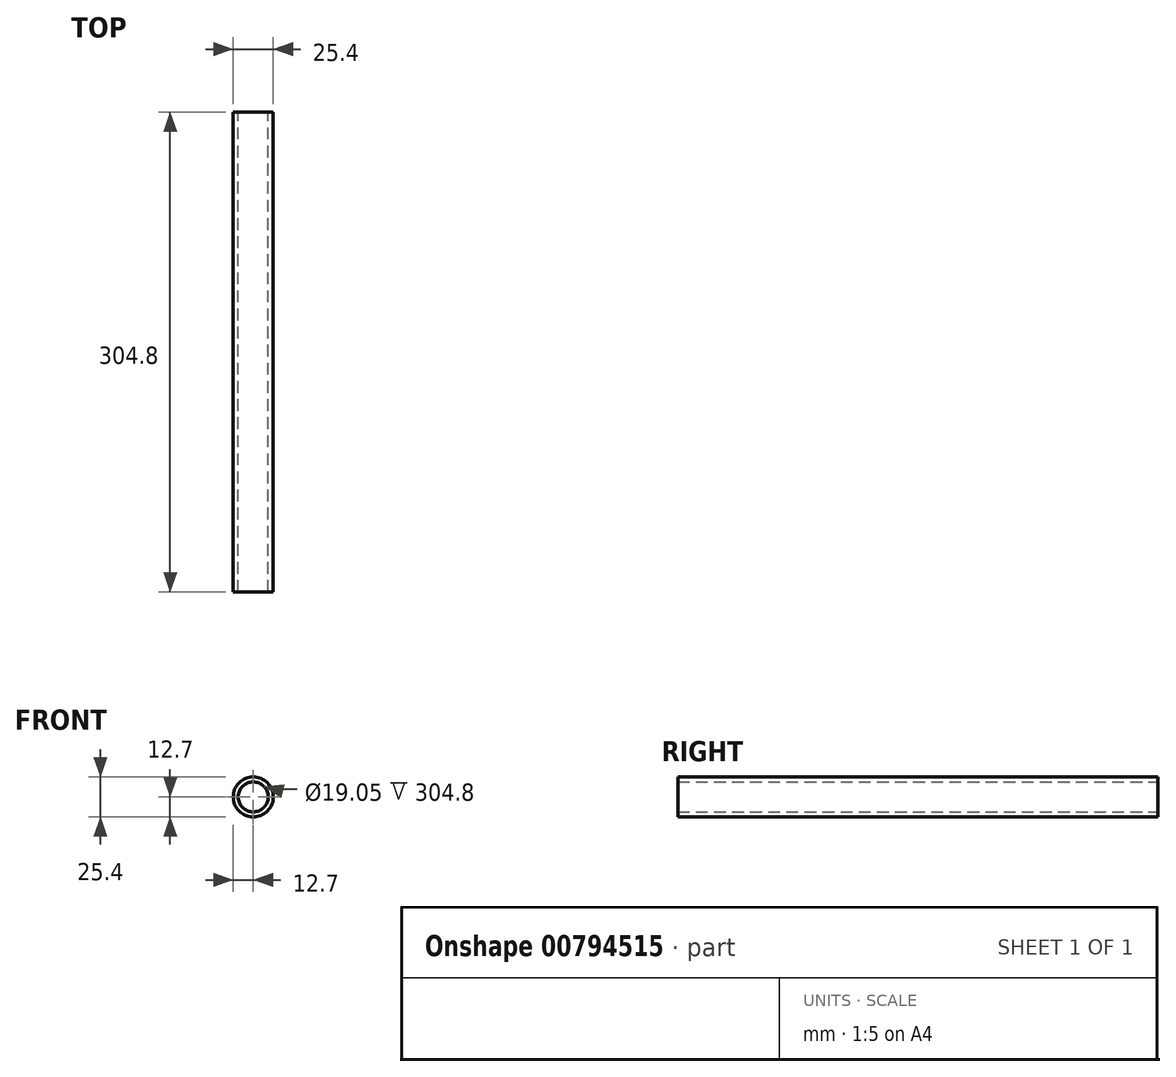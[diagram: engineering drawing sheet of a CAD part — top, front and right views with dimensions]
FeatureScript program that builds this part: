
annotation { "Feature Type Name" : "Feature", "Feature Type Description" : "" }
export const myFeature = defineFeature(function(context is Context, id is Id, definition is map)
    precondition{}
    {
        {
            var Q0;
            Q0=qCreatedBy(makeId("Front.planeOp"),FACE);
            var sketch = newSketch(context, id + "F0", { "sketchPlane" : qUnion([Q0])});
            skCircle(sketch, "E0", {"center": v(0, 0) * mm, "radius": 12.7 * mm});
            skCircle(sketch, "E1", {"center": v(0, 0) * mm, "radius": 9.53 * mm});
            skSolve(sketch);
        }
        {
            var Q0;
            Q0=makeQuery(id+"F0.imprint","IMPRINT",FACE,{"disambiguationData":[TD([[makeQuery(id+"F0.imprint","IMPRINT",EDGE,{"derivedFrom":sQuery(id+"F0.wireOp",EDGE,"E0")}),1.0]])]});
            extrude(context, id + "F1", {"entities" : qUnion([Q0]), "endBound" : BoundingType.SYMMETRIC, "depth" : 304.8 * mm, "offsetDistance" : 25.4 * mm});
        }
    });
